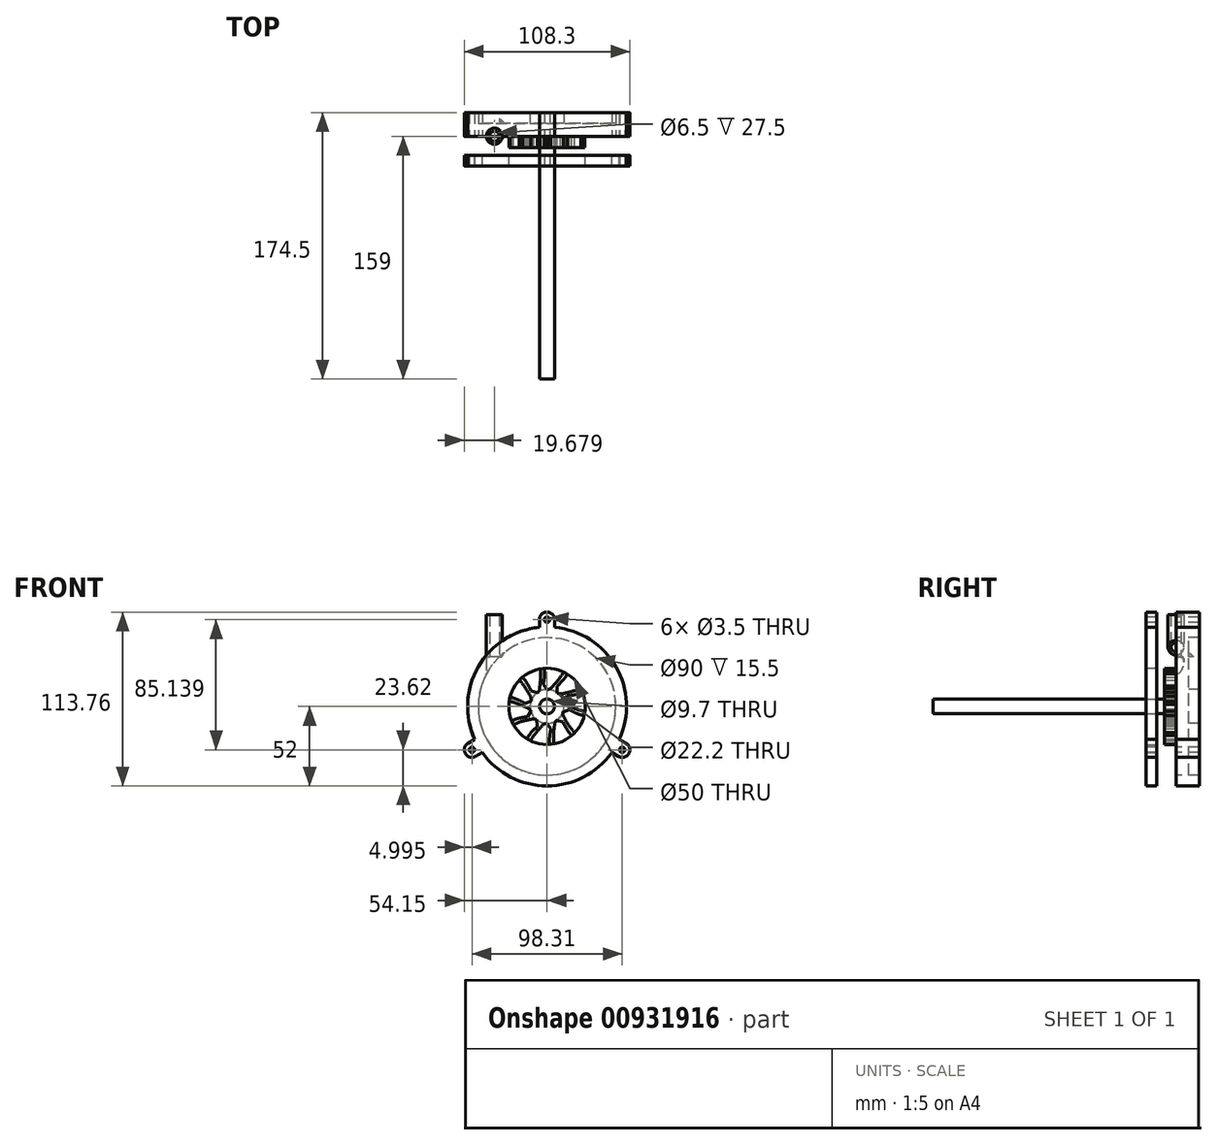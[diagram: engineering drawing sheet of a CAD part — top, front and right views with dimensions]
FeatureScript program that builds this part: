
annotation { "Feature Type Name" : "Feature", "Feature Type Description" : "" }
export const myFeature = defineFeature(function(context is Context, id is Id, definition is map)
    precondition{}
    {
        {
            var Q0;
            Q0=qCreatedBy(makeId("Front.planeOp"),FACE);
            var sketch = newSketch(context, id + "F0", { "sketchPlane" : qUnion([Q0]), "disableImprinting" : false});
            skCircle(sketch, "E0", {"center": v(0, 0) * mm, "radius": 4.85 * mm});
            skCircle(sketch, "E1.0", {"center": v(0, 0) * mm, "radius": 10.85 * mm});
            skFitSpline(sketch, "E2", {"points": [v(-10.85, 0) * mm, v(-26.63, 6.23) * mm, v(-42.34, 0) * mm], "startDerivative": vector(-31.74, 18.78) * mm, "endDerivative": vector(-33.68, -18.59) * mm});
            skLineSegment(sketch, "E3", {"start": v(-42.34, 0) * mm, "end": v(-42.16, -2) * mm});
            skFitSpline(sketch, "E4", {"points": [v(-42.16, -2) * mm, v(-27.23, 3.48) * mm, v(-10.67, -2) * mm], "startDerivative": vector(30.43, 14.98) * mm, "endDerivative": vector(25.07, -11.68) * mm});
            skLineSegment(sketch, "E5", {"start": v(-10.85, 0) * mm, "end": v(-10.67, -2) * mm});
            skSolve(sketch);
        }
        {
            var Q0;
            {var subQ1=sQuery(id+"F0.wireOp",EDGE,"E2");Q0=makeQuery(id+"F0.imprint","IMPRINT",FACE,{"disambiguationData":[TD([[makeQuery(id+"F0.imprint","IMPRINT",EDGE,{"derivedFrom":subQ1}),1.0]])]});}
            var Q1;
            {var subQ0=sQuery(id+"F0.wireOp",EDGE,"E5");Q1=makeQuery(id+"F0.imprint","IMPRINT",FACE,{"disambiguationData":[TD([[makeQuery(id+"F0.imprint","IMPRINT",EDGE,{"derivedFrom":subQ0}),-1.0]])]});}
            extrude(context, id + "F1", {"entities" : qUnion([Q0, Q1]), "depth" : 15 * mm, "offsetDistance" : 25 * mm, "symmetric" : true});
        }
        {
            var Q0;
            Q0=makeQuery(id+"F0.imprint","IMPRINT",FACE,{"disambiguationData":[TD([[makeQuery(id+"F0.imprint","IMPRINT",EDGE,{"derivedFrom":sQuery(id+"F0.wireOp",EDGE,"E0")}),-1.0]])]});
            extrude(context, id + "F2", {"entities" : qUnion([Q0]), "operationType" : NewBodyOperationType.ADD, "depth" : 15 * mm, "offsetDistance" : 25 * mm, "symmetric" : true});
        }
        {
            var Q0;
            {var subQ0=sQuery(id+"F0.wireOp",EDGE,"E5");var subQ1=sQuery(id+"F0.wireOp",EDGE,"E4");var subQ2=sQuery(id+"F0.wireOp",EDGE,"E1.0");Q0=makeQuery(id+"F2.boolean.opBoolean","MERGE",EDGE,{"derivedFrom":[makeQuery(id+"F1.opExtrude","SWEPT_EDGE",EDGE,{"disambiguationData":[OSD([subQ2,subQ1,subQ0])]}),makeQuery(id+"F2.opExtrude","SWEPT_EDGE",EDGE,{"disambiguationData":[OSD([subQ2,subQ1,subQ0])]})]});}
            var Q1;
            {var subQ0=sQuery(id+"F0.wireOp",EDGE,"E5");var subQ1=sQuery(id+"F0.wireOp",EDGE,"E2");var subQ2=sQuery(id+"F0.wireOp",EDGE,"E1.0");Q1=makeQuery(id+"F2.boolean.opBoolean","MERGE",EDGE,{"derivedFrom":[makeQuery(id+"F1.opExtrude","SWEPT_EDGE",EDGE,{"disambiguationData":[OSD([subQ2,subQ1,subQ0])]}),makeQuery(id+"F2.opExtrude","SWEPT_EDGE",EDGE,{"disambiguationData":[OSD([subQ2,subQ1,subQ0])]})]});}
            chamfer(context, id + "F3", {"entities" : qUnion([Q0, Q1]), "width" : 3 * mm, "tangentPropagation" : true});
        }
        {
            var Q0;
            Q0=makeQuery(id+"F1.opExtrude","SWEPT_BODY",BODY,{"disambiguationData":[OSD([sQuery(id+"F0.wireOp",EDGE,"E2"),sQuery(id+"F0.wireOp",EDGE,"E3"),sQuery(id+"F0.wireOp",EDGE,"E4"),sQuery(id+"F0.wireOp",EDGE,"E5")])]});
            var Q1;
            Q1=makeQuery(id+"F2.opExtrude","CAP_EDGE",EDGE,{"disambiguationData":[OSD([sQuery(id+"F0.wireOp",EDGE,"E0")])],"isStart":false});
            circularPattern(context, id + "F4", {"operationType" : NewBodyOperationType.ADD, "entities" : qUnion([Q0]), "axis" : qUnion([Q1]), "angle" : 360 * degree, "instanceCount" : 10, "equalSpace" : true});
        }
        {
            var Q0;
            Q0=qCreatedBy(makeId("Front.planeOp"),FACE);
            var sketch = newSketch(context, id + "F5", { "sketchPlane" : qUnion([Q0])});
            skCircle(sketch, "E6", {"center": v(0, 0) * mm, "radius": 45 * mm});
            skCircle(sketch, "E7.0", {"center": v(0, 0) * mm, "radius": 52 * mm});
            skCircle(sketch, "E8", {"center": v(0, 0) * mm, "radius": 25 * mm});
            skCircle(sketch, "E9.0", {"center": v(0, 0) * mm, "radius": 44.7 * mm});
            skSolve(sketch);
        }
        {
            var Q0;
            Q0=makeQuery(id+"F5.imprint","IMPRINT",FACE,{"disambiguationData":[TD([[makeQuery(id+"F5.imprint","IMPRINT",EDGE,{"derivedFrom":sQuery(id+"F5.wireOp",EDGE,"E6")}),-1.0]])]});
            extrude(context, id + "F6", {"entities" : qUnion([Q0]), "oppositeDirection" : true, "depth" : 15.5 * mm, "offsetDistance" : 25 * mm, "hasSecondDirection" : true, "secondDirectionOppositeDirection" : false, "secondDirectionDepth" : 12.5 * mm});
        }
        {
            var Q0;
            Q0=qCreatedBy(makeId("Top.planeOp"),FACE);
            var sketch = newSketch(context, id + "F7", { "sketchPlane" : qUnion([Q0])});
            skCircle(sketch, "E10", {"center": v(-34.47, 0) * mm, "radius": 5.25 * mm});
            skCircle(sketch, "E11.0", {"center": v(-34.47, 0) * mm, "radius": 3.25 * mm});
            skSolve(sketch);
        }
        {
            var Q0;
            Q0 = qSketchRegion(id + "F7", true);
            extrude(context, id + "F8", {"entities" : qUnion([Q0]), "operationType" : NewBodyOperationType.ADD, "depth" : 60 * mm, "offsetDistance" : 25 * mm});
        }
        {
            var Q0;
            Q0 = qSketchRegion(id + "F7", true);
            extrude(context, id + "F9", {"entities" : qUnion([Q0]), "operationType" : NewBodyOperationType.REMOVE, "depth" : 32.5 * mm, "offsetDistance" : 25 * mm});
        }
        {
            var Q0;
            Q0=makeQuery(id+"F7.imprint","IMPRINT",FACE,{"disambiguationData":[TD([[makeQuery(id+"F7.imprint","IMPRINT",EDGE,{"derivedFrom":sQuery(id+"F7.wireOp",EDGE,"E11.0")}),1.0]])]});
            extrude(context, id + "F10", {"entities" : qUnion([Q0]), "operationType" : NewBodyOperationType.REMOVE, "depth" : 61.1 * mm, "offsetDistance" : 25 * mm});
        }
        {
            var Q0;
            {var subQ0=sQuery(id+"F7.wireOp",EDGE,"E10");Q0=makeQuery(id+"F9.boolean.opBoolean","COPY",EDGE,{"disambiguationData":[topologyDisambiguationEdgeConnected([makeQuery(id+"F8.opExtrude","SWEPT_FACE",FACE,{"disambiguationData":[OSD([subQ0])]})])],"derivedFrom":makeQuery(id+"F9.opExtrude","CAP_EDGE",EDGE,{"disambiguationData":[OSD([subQ0])],"isStart":false})});}
            fillet(context, id + "F11", {"entities" : qUnion([Q0]), "radius" : 1.5 * mm, "tangentPropagation" : true, "allowEdgeOverflow" : false});
        }
        {
            var Q0;
            {var subQ0=makeQuery(id+"F6.opExtrude","SWEPT_FACE",FACE,{"disambiguationData":[OSD([sQuery(id+"F5.wireOp",EDGE,"E6")])]});var subQ1=sQuery(id+"F7.wireOp",EDGE,"E10");Q0=makeQuery(id+"F9.boolean.opBoolean","SPLIT",EDGE,{"disambiguationData":[topologyDisambiguationEdgeConnected([makeQuery(id+"F9.opExtrude","SWEPT_FACE",FACE,{"disambiguationData":[OSD([subQ1])]})])],"derivedFrom":makeQuery(id+"F8.boolean.opBoolean","INTERSECT",EDGE,{"derivedFrom":[subQ0,makeQuery(id+"F8.opExtrude","SWEPT_FACE",FACE,{"disambiguationData":[OSD([subQ1])]})]})});}
            chamfer(context, id + "F12", {"entities" : qUnion([Q0]), "width" : 10 * mm, "tangentPropagation" : true});
        }
        {
            var Q0;
            Q0=qCreatedBy(makeId("Front.planeOp"),FACE);
            var sketch = newSketch(context, id + "F13", { "sketchPlane" : qUnion([Q0])});
            skCircle(sketch, "E12", {"center": v(0, 0) * mm, "radius": 4.85 * mm});
            skSolve(sketch);
        }
        {
            var Q0;
            Q0=makeQuery(id+"F13.imprint","IMPRINT",FACE,{"disambiguationData":[TD([[makeQuery(id+"F13.imprint","IMPRINT",EDGE,{"derivedFrom":sQuery(id+"F13.wireOp",EDGE,"E12")}),1.0]])]});
            extrude(context, id + "F14", {"entities" : qUnion([Q0]), "depth" : 159 * mm, "offsetDistance" : 25 * mm, "hasSecondDirection" : true, "secondDirectionOppositeDirection" : true, "secondDirectionDepth" : 15.5 * mm});
        }
        {
            var Q0;
            Q0=makeQuery(id+"F5.imprint","IMPRINT",FACE,{"disambiguationData":[TD([[makeQuery(id+"F5.imprint","IMPRINT",EDGE,{"derivedFrom":sQuery(id+"F5.wireOp",EDGE,"E8")}),-1.0]])]});
            var Q1;
            Q1=makeQuery(id+"F5.imprint","IMPRINT",FACE,{"disambiguationData":[TD([[makeQuery(id+"F5.imprint","IMPRINT",EDGE,{"derivedFrom":sQuery(id+"F5.wireOp",EDGE,"E6")}),1.0]])]});
            var Q2;
            Q2=makeQuery(id+"F5.imprint","IMPRINT",FACE,{"disambiguationData":[TD([[makeQuery(id+"F5.imprint","IMPRINT",EDGE,{"derivedFrom":sQuery(id+"F5.wireOp",EDGE,"E8")}),1.0]])]});
            extrude(context, id + "F15", {"entities" : qUnion([Q0, Q1, Q2]), "oppositeDirection" : true, "depth" : 15.5 * mm, "offsetDistance" : 25 * mm});
        }
        {
            var Q0;
            Q0=makeQuery(id+"F5.imprint","IMPRINT",FACE,{"disambiguationData":[TD([[makeQuery(id+"F5.imprint","IMPRINT",EDGE,{"derivedFrom":sQuery(id+"F5.wireOp",EDGE,"E8")}),-1.0]])]});
            var Q1;
            Q1=makeQuery(id+"F5.imprint","IMPRINT",FACE,{"disambiguationData":[TD([[makeQuery(id+"F5.imprint","IMPRINT",EDGE,{"derivedFrom":sQuery(id+"F5.wireOp",EDGE,"E6")}),1.0]])]});
            var Q2;
            Q2=makeQuery(id+"F5.imprint","IMPRINT",FACE,{"disambiguationData":[TD([[makeQuery(id+"F5.imprint","IMPRINT",EDGE,{"derivedFrom":sQuery(id+"F5.wireOp",EDGE,"E8")}),1.0]])]});
            extrude(context, id + "F16", {"entities" : qUnion([Q0, Q1, Q2]), "operationType" : NewBodyOperationType.REMOVE, "oppositeDirection" : true, "depth" : 8.5 * mm, "offsetDistance" : 25 * mm});
        }
        {
            var Q0;
            Q0=qCreatedBy(makeId("Front.planeOp"),FACE);
            var sketch = newSketch(context, id + "F17", { "sketchPlane" : qUnion([Q0])});
            skCircle(sketch, "E13", {"center": v(0, 0) * mm, "radius": 11.1 * mm});
            skSolve(sketch);
        }
        {
            var Q0;
            Q0=makeQuery(id+"F17.imprint","IMPRINT",FACE,{"disambiguationData":[TD([[makeQuery(id+"F17.imprint","IMPRINT",EDGE,{"derivedFrom":sQuery(id+"F17.wireOp",EDGE,"E13")}),1.0]])]});
            extrude(context, id + "F18", {"entities" : qUnion([Q0]), "operationType" : NewBodyOperationType.REMOVE, "oppositeDirection" : true, "depth" : 25 * mm, "offsetDistance" : 25 * mm});
        }
        {
            var Q0;
            Q0=makeQuery(id+"F5.imprint","IMPRINT",FACE,{"disambiguationData":[TD([[makeQuery(id+"F5.imprint","IMPRINT",EDGE,{"derivedFrom":sQuery(id+"F5.wireOp",EDGE,"E8")}),-1.0]])]});
            var Q1;
            Q1=makeQuery(id+"F5.imprint","IMPRINT",FACE,{"disambiguationData":[TD([[makeQuery(id+"F5.imprint","IMPRINT",EDGE,{"derivedFrom":sQuery(id+"F5.wireOp",EDGE,"E6")}),-1.0]])]});
            var Q2;
            Q2=makeQuery(id+"F5.imprint","IMPRINT",FACE,{"disambiguationData":[TD([[makeQuery(id+"F5.imprint","IMPRINT",EDGE,{"derivedFrom":sQuery(id+"F5.wireOp",EDGE,"E6")}),1.0]])]});
            extrude(context, id + "F19", {"entities" : qUnion([Q0, Q1, Q2]), "depth" : 19.5 * mm, "offsetDistance" : 25 * mm});
        }
        {
            var Q0;
            Q0=makeQuery(id+"F5.imprint","IMPRINT",FACE,{"disambiguationData":[TD([[makeQuery(id+"F5.imprint","IMPRINT",EDGE,{"derivedFrom":sQuery(id+"F5.wireOp",EDGE,"E8")}),-1.0]])]});
            var Q1;
            Q1=makeQuery(id+"F5.imprint","IMPRINT",FACE,{"disambiguationData":[TD([[makeQuery(id+"F5.imprint","IMPRINT",EDGE,{"derivedFrom":sQuery(id+"F5.wireOp",EDGE,"E6")}),1.0]])]});
            var Q2;
            Q2=makeQuery(id+"F5.imprint","IMPRINT",FACE,{"disambiguationData":[TD([[makeQuery(id+"F5.imprint","IMPRINT",EDGE,{"derivedFrom":sQuery(id+"F5.wireOp",EDGE,"E6")}),-1.0]])]});
            extrude(context, id + "F20", {"entities" : qUnion([Q0, Q1, Q2]), "operationType" : NewBodyOperationType.REMOVE, "depth" : 12.5 * mm, "offsetDistance" : 25 * mm});
        }
        {
            var Q0;
            Q0=qCreatedBy(makeId("Front.planeOp"),FACE);
            var sketch = newSketch(context, id + "F21", { "sketchPlane" : qUnion([Q0])});
            skCircle(sketch, "E14", {"center": v(0, 0) * mm, "radius": 52 * mm});
            skLineSegment(sketch, "E15.bottom", {"start": v(0, 61.76) * mm, "end": v(0, 61.76) * mm});
            skLineSegment(sketch, "E15.top", {"start": v(5, 51.76) * mm, "end": v(-5, 51.76) * mm});
            skLineSegment(sketch, "E15.left", {"start": v(5, 56.76) * mm, "end": v(5, 51.76) * mm});
            skLineSegment(sketch, "E15.right", {"start": v(-5, 56.76) * mm, "end": v(-5, 51.76) * mm});
            skPoint(sketch, "E15.middle", {"position": v(0, 52) * mm});
            skCircle(sketch, "E16", {"center": v(0, 56.76) * mm, "radius": 1.75 * mm});
            skPoint(sketch, "E17.visualSharp", {"position": v(-5, 61.76) * mm});
            skArc(sketch, "E17.filletArc", {"start": v(0, 61.76) * mm, "mid": v(-3.54, 60.3) * mm, "end": v(-5, 56.76) * mm});
            skPoint(sketch, "E18.visualSharp", {"position": v(5, 61.76) * mm});
            skArc(sketch, "E18.filletArc", {"start": v(5, 56.76) * mm, "mid": v(3.54, 60.3) * mm, "end": v(0, 61.76) * mm});
            skArc(sketch, "E19.1.0", {"start": v(-53.48, -30.88) * mm, "mid": v(-50.45, -33.2) * mm, "end": v(-46.65, -32.7) * mm});
            skLineSegment(sketch, "E19.1.1", {"start": v(-46.65, -32.7) * mm, "end": v(-42.32, -30.2) * mm});
            skLineSegment(sketch, "E19.1.2", {"start": v(-47.32, -21.55) * mm, "end": v(-42.32, -30.2) * mm});
            skLineSegment(sketch, "E19.1.3", {"start": v(-51.65, -24.05) * mm, "end": v(-47.32, -21.55) * mm});
            skArc(sketch, "E19.1.4", {"start": v(-51.65, -24.05) * mm, "mid": v(-53.98, -27.09) * mm, "end": v(-53.48, -30.88) * mm});
            skCircle(sketch, "E19.1.5", {"center": v(-49.15, -28.38) * mm, "radius": 1.75 * mm});
            skArc(sketch, "E19.2.0", {"start": v(53.48, -30.88) * mm, "mid": v(53.98, -27.09) * mm, "end": v(51.65, -24.05) * mm});
            skLineSegment(sketch, "E19.2.1", {"start": v(51.65, -24.05) * mm, "end": v(47.32, -21.55) * mm});
            skLineSegment(sketch, "E19.2.2", {"start": v(42.32, -30.2) * mm, "end": v(47.32, -21.55) * mm});
            skLineSegment(sketch, "E19.2.3", {"start": v(46.65, -32.7) * mm, "end": v(42.32, -30.2) * mm});
            skArc(sketch, "E19.2.4", {"start": v(46.65, -32.7) * mm, "mid": v(50.45, -33.2) * mm, "end": v(53.48, -30.88) * mm});
            skCircle(sketch, "E19.2.5", {"center": v(49.15, -28.38) * mm, "radius": 1.75 * mm});
            skSolve(sketch);
        }
        {
            var Q0;
            Q0=makeQuery(id+"F21.imprint","IMPRINT",FACE,{"disambiguationData":[TD([[makeQuery(id+"F21.imprint","IMPRINT",EDGE,{"derivedFrom":sQuery(id+"F21.wireOp",EDGE,"E19.1.0")}),1.0]])]});
            var Q1;
            {var subQ1=sQuery(id+"F21.wireOp",EDGE,"E15.left");Q1=makeQuery(id+"F21.imprint","IMPRINT",FACE,{"disambiguationData":[TD([[makeQuery(id+"F21.imprint","IMPRINT",EDGE,{"derivedFrom":subQ1}),-1.0]])]});}
            var Q2;
            Q2=makeQuery(id+"F21.imprint","IMPRINT",FACE,{"disambiguationData":[TD([[makeQuery(id+"F21.imprint","IMPRINT",EDGE,{"derivedFrom":sQuery(id+"F21.wireOp",EDGE,"E19.2.0")}),1.0]])]});
            extrude(context, id + "F22", {"entities" : qUnion([Q0, Q1, Q2]), "operationType" : NewBodyOperationType.ADD, "oppositeDirection" : true, "depth" : 15.5 * mm, "offsetDistance" : 25 * mm, "hasSecondDirection" : true, "secondDirectionOppositeDirection" : false, "secondDirectionDepth" : 12 * mm});
        }
        {
            var Q0;
            Q0=makeQuery(id+"F21.imprint","IMPRINT",FACE,{"disambiguationData":[TD([[makeQuery(id+"F21.imprint","IMPRINT",EDGE,{"derivedFrom":sQuery(id+"F21.wireOp",EDGE,"E19.1.0")}),1.0]])]});
            var Q1;
            {var subQ1=sQuery(id+"F21.wireOp",EDGE,"E15.left");Q1=makeQuery(id+"F21.imprint","IMPRINT",FACE,{"disambiguationData":[TD([[makeQuery(id+"F21.imprint","IMPRINT",EDGE,{"derivedFrom":subQ1}),-1.0]])]});}
            var Q2;
            Q2=makeQuery(id+"F21.imprint","IMPRINT",FACE,{"disambiguationData":[TD([[makeQuery(id+"F21.imprint","IMPRINT",EDGE,{"derivedFrom":sQuery(id+"F21.wireOp",EDGE,"E19.2.0")}),1.0]])]});
            extrude(context, id + "F23", {"entities" : qUnion([Q0, Q1, Q2]), "operationType" : NewBodyOperationType.ADD, "depth" : 19.5 * mm, "offsetDistance" : 25 * mm});
        }
        {
            var Q0;
            Q0=makeQuery(id+"F21.imprint","IMPRINT",FACE,{"disambiguationData":[TD([[makeQuery(id+"F21.imprint","IMPRINT",EDGE,{"derivedFrom":sQuery(id+"F21.wireOp",EDGE,"E19.1.0")}),1.0]])]});
            var Q1;
            Q1=makeQuery(id+"F21.imprint","IMPRINT",FACE,{"disambiguationData":[TD([[makeQuery(id+"F21.imprint","IMPRINT",EDGE,{"derivedFrom":sQuery(id+"F21.wireOp",EDGE,"E19.2.0")}),1.0]])]});
            var Q2;
            {var subQ1=sQuery(id+"F21.wireOp",EDGE,"E15.left");Q2=makeQuery(id+"F21.imprint","IMPRINT",FACE,{"disambiguationData":[TD([[makeQuery(id+"F21.imprint","IMPRINT",EDGE,{"derivedFrom":subQ1}),-1.0]])]});}
            extrude(context, id + "F24", {"entities" : qUnion([Q0, Q1, Q2]), "operationType" : NewBodyOperationType.REMOVE, "depth" : 12.5 * mm, "offsetDistance" : 25 * mm});
        }
    });
